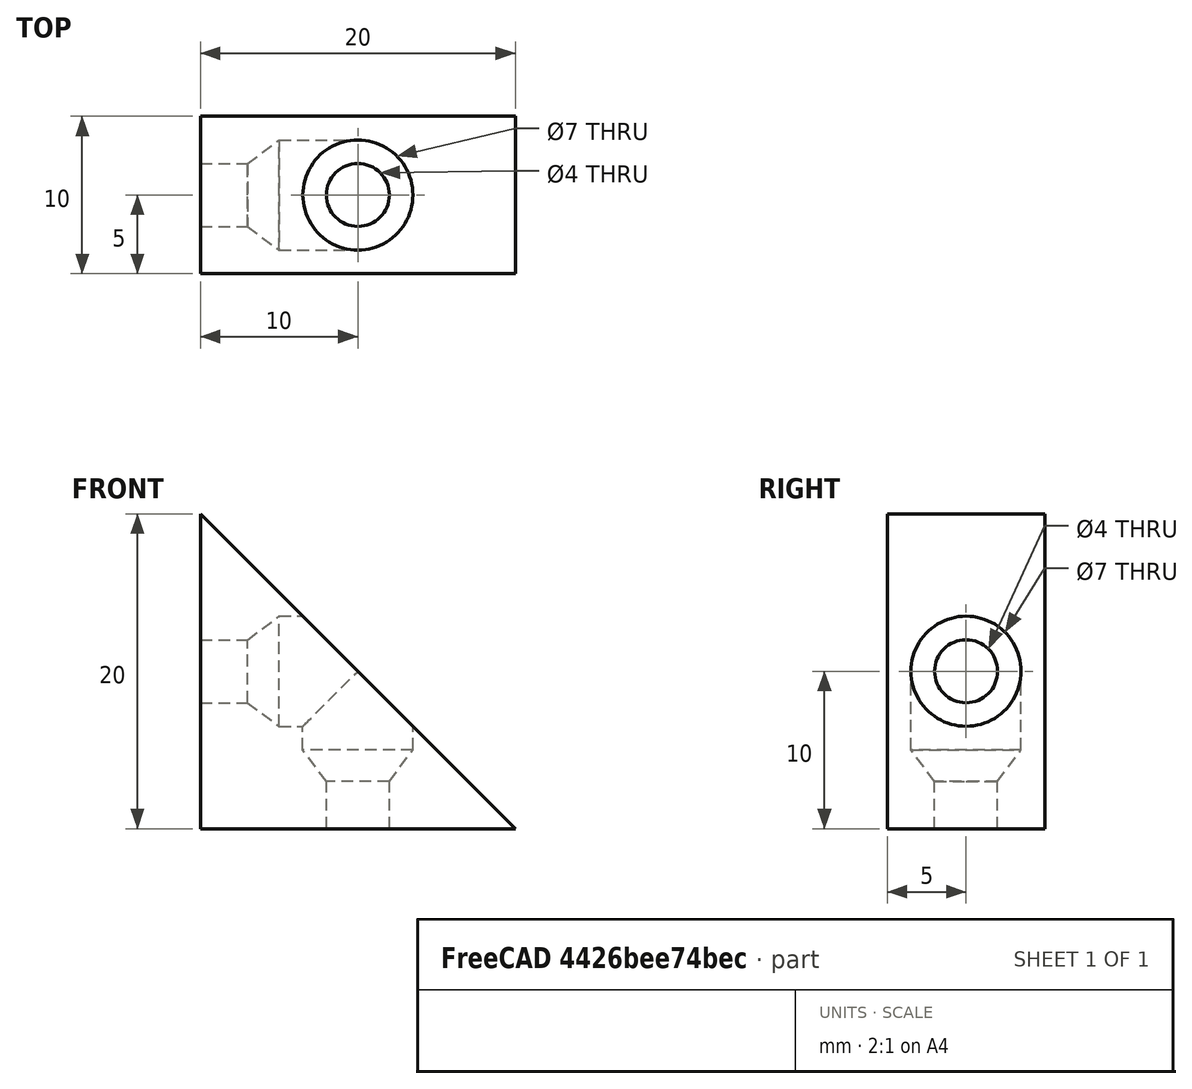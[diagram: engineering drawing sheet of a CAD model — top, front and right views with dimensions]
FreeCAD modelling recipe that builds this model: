
FCSTD DOCUMENT  (FreeCAD 0.16R6703 (Git))
Label: Escuadra Delantera
License: All rights reserved
LicenseURL: http://en.wikipedia.org/wiki/All_rights_reserved
objects: Part::MultiFuse×3, Part::Cylinder×2, Part::Wedge×1, Part::Cone×1, Part::Cut×1
note: 8 computed .brp shape members not serialized (recipe doc carries the construction recipe); baked Part::Feature solids carry a one-line shape summary decoded from their .brp

FEATURE [Part::Wedge] Wedge
  Placement = pos=(0,0,0) rot=(0,0,-1;1.5708rad)
  X2max = 10
  X2min = 0
  Xmax = 10
  Xmin = 0
  Ymax = 20
  Ymin = 0
  Z2max = 0
  Z2min = 0
  Zmax = 20
  Zmin = 0
FEATURE [Part::Cylinder] Cylinder
  Angle = 360
  Height = 10
  Placement = pos=(15,-5,0) rot=(0,0,1;0rad)
  Radius = 2
FEATURE [Part::Cylinder] Cylinder001
  Angle = 360
  Height = 10
  Placement = pos=(15,-5,5) rot=(0,0,1;0rad)
  Radius = 3.5
FEATURE [Part::Cone] Cone
  Angle = 360
  Height = 2
  Placement = pos=(15,-5,3) rot=(0,0,1;0rad)
  Radius1 = 2
  Radius2 = 3.5
FEATURE [Part::MultiFuse] Fusion
  Placement = pos=(0,0,25) rot=(0,1,0;1.5708rad)
  Shapes = -> [Cylinder,Cylinder001,Cone]
FEATURE [Part::MultiFuse] Fusion001
  Placement = pos=(-5,0,0) rot=(0,0,1;0rad)
  Shapes = -> [Cylinder,Cylinder001,Cone]
FEATURE [Part::MultiFuse] Fusion002
  Shapes = -> [Fusion001,Fusion]
FEATURE [Part::Cut] Cut
  Base = -> Wedge
  Tool = -> Fusion002
